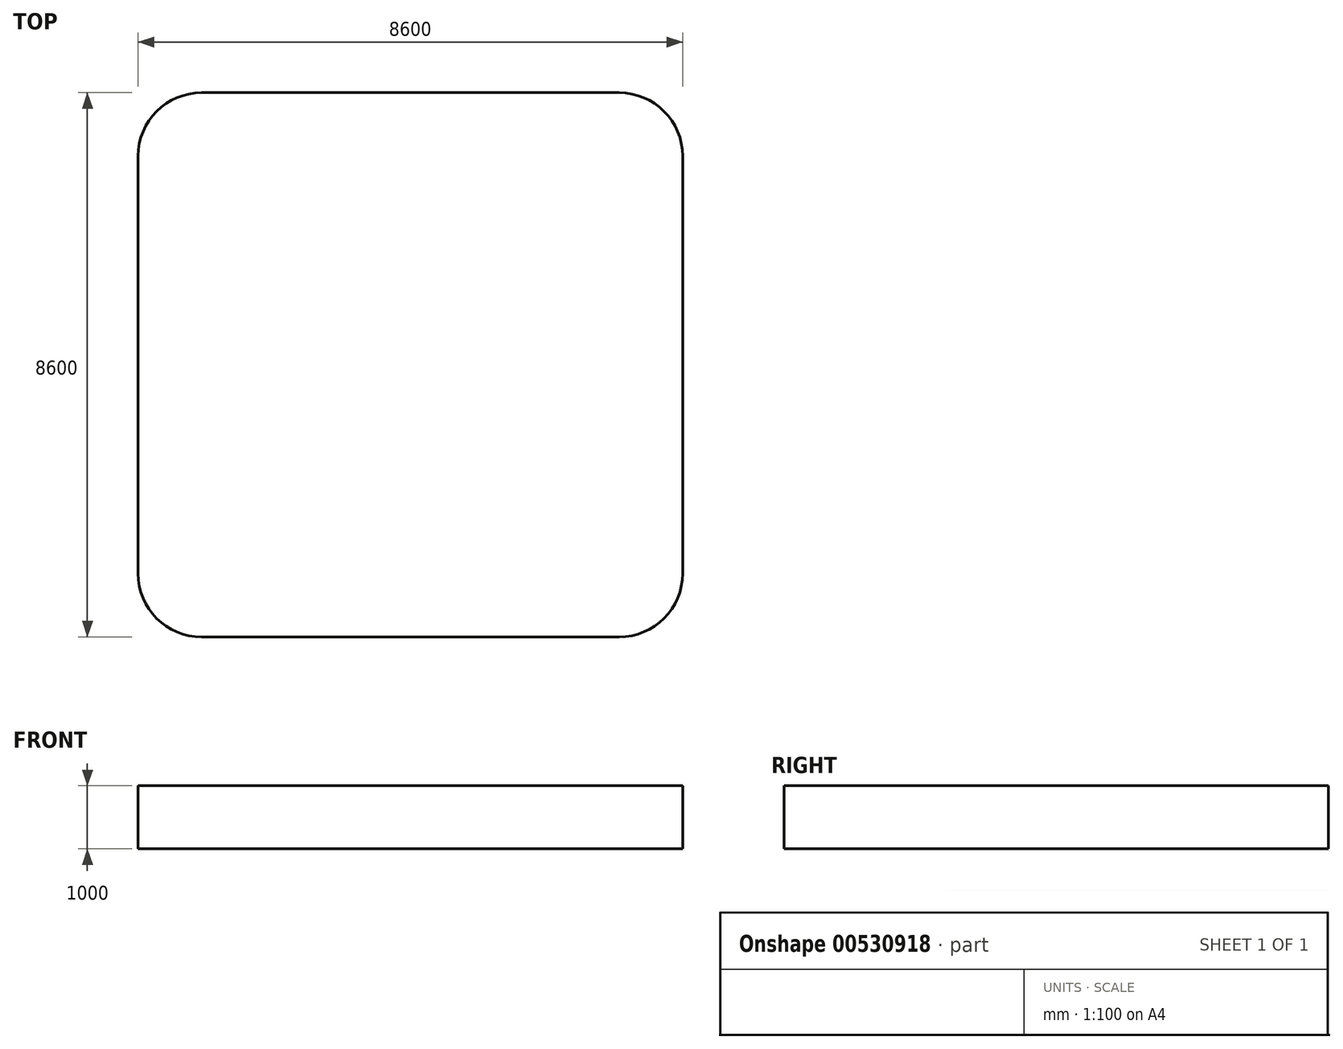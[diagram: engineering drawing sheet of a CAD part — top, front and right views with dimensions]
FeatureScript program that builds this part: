
annotation { "Feature Type Name" : "Feature", "Feature Type Description" : "" }
export const myFeature = defineFeature(function(context is Context, id is Id, definition is map)
    precondition{}
    {
        {
            var Q0;
            Q0=qCreatedBy(makeId("Top.planeOp"),FACE);
            var sketch = newSketch(context, id + "F0", { "sketchPlane" : qUnion([Q0])});
            skLineSegment(sketch, "E0.bottom", {"start": v(3300, 4300) * mm, "end": v(-3300, 4300) * mm});
            skLineSegment(sketch, "E0.top", {"start": v(3300, -4300) * mm, "end": v(-3300, -4300) * mm});
            skLineSegment(sketch, "E0.left", {"start": v(4300, 3300) * mm, "end": v(4300, -3300) * mm});
            skLineSegment(sketch, "E0.right", {"start": v(-4300, 3300) * mm, "end": v(-4300, -3300) * mm});
            skPoint(sketch, "E0.middle", {"position": v(0, 0) * mm});
            skPoint(sketch, "E1.visualSharp", {"position": v(-4300, 4300) * mm});
            skArc(sketch, "E1.filletArc", {"start": v(-3300, 4300) * mm, "mid": v(-4007.1, 4007.1) * mm, "end": v(-4300, 3300) * mm});
            skPoint(sketch, "E2.visualSharp", {"position": v(4300, 4300) * mm});
            skArc(sketch, "E2.filletArc", {"start": v(4300, 3300) * mm, "mid": v(4007.1, 4007.1) * mm, "end": v(3300, 4300) * mm});
            skPoint(sketch, "E3.visualSharp", {"position": v(-4300, -4300) * mm});
            skArc(sketch, "E3.filletArc", {"start": v(-4300, -3300) * mm, "mid": v(-4007.1, -4007.1) * mm, "end": v(-3300, -4300) * mm});
            skPoint(sketch, "E4.visualSharp", {"position": v(4300, -4300) * mm});
            skArc(sketch, "E4.filletArc", {"start": v(3300, -4300) * mm, "mid": v(4007.1, -4007.1) * mm, "end": v(4300, -3300) * mm});
            skSolve(sketch);
        }
        {
            var Q0;
            Q0=makeQuery(id+"F0.imprint","IMPRINT",FACE,{"disambiguationData":[TD([[makeQuery(id+"F0.imprint","IMPRINT",EDGE,{"derivedFrom":sQuery(id+"F0.wireOp",EDGE,"E0.bottom")}),1.0]])]});
            extrude(context, id + "F1", {"entities" : qUnion([Q0]), "depth" : 1000 * mm, "offsetDistance" : 25 * mm});
        }
    });
